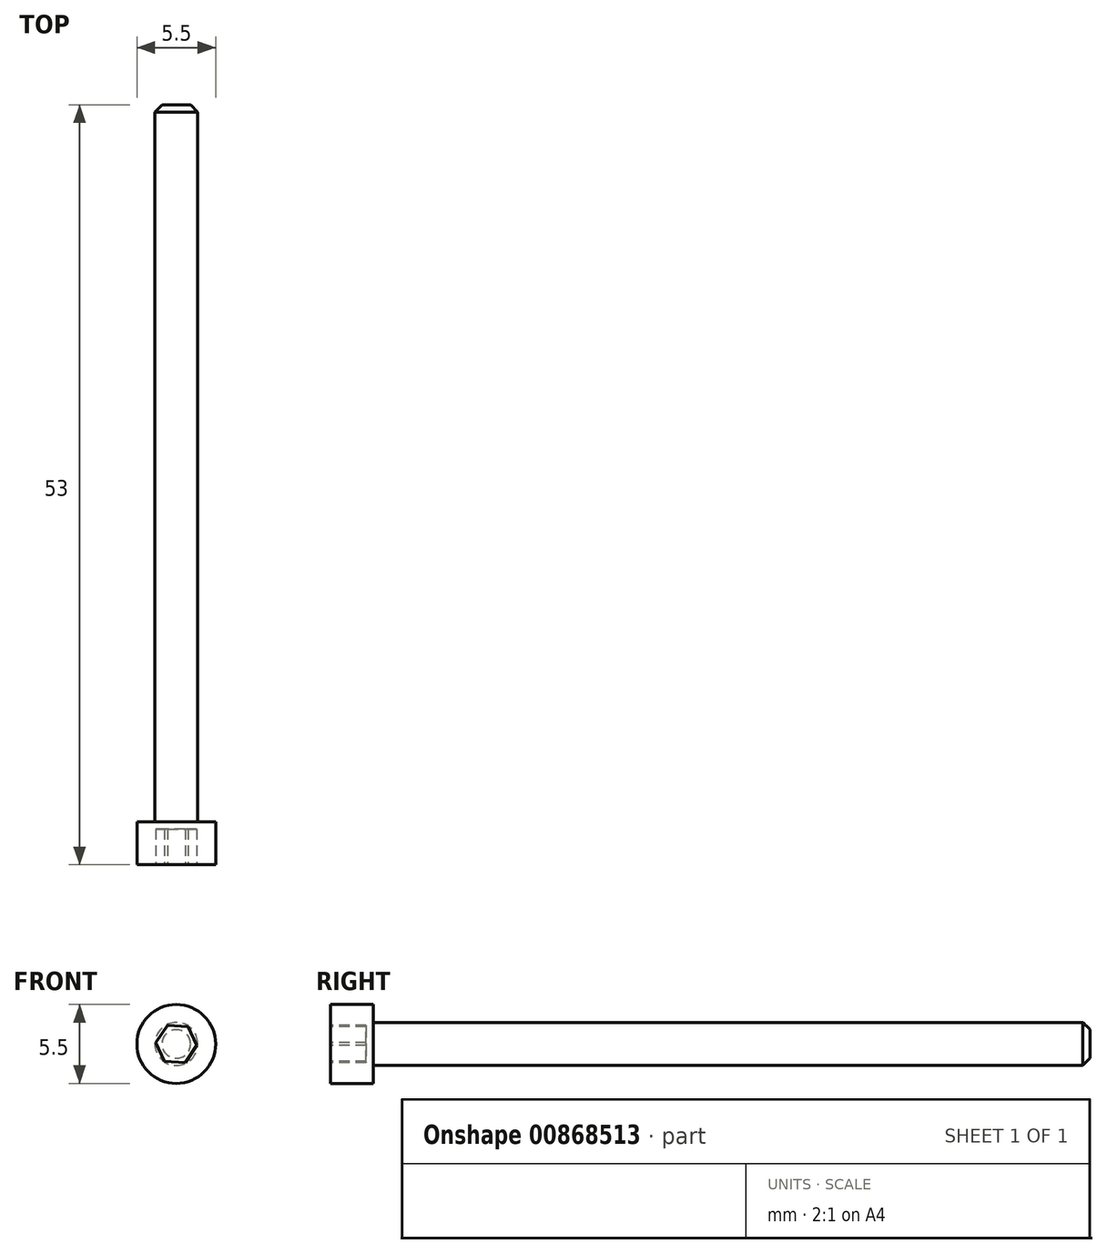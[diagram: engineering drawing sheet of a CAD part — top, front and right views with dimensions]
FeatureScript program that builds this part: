
annotation { "Feature Type Name" : "Feature", "Feature Type Description" : "" }
export const myFeature = defineFeature(function(context is Context, id is Id, definition is map)
    precondition{}
    {
        {
            assignVariable(context, id + "F0", {"name" : "Metric", "anyValue" : 3});
        }
        {
            assignVariable(context, id + "F1", {"name" : "Lenght", "anyValue" : 50});
        }
        {
            assignVariable(context, id + "F2", {"name" : "k", "anyValue" : [0, 1, 2, 3, 4, 5, 6, 0, 8][getVariable(context, 'Metric')]});
        }
        {
            var Q0;
            Q0=qCreatedBy(makeId("Front.planeOp"),FACE);
            var sketch = newSketch(context, id + "F3", { "sketchPlane" : qUnion([Q0])});
            skCircle(sketch, "E0", {"center": v(0, 0) * mm, "radius": 2.75 * mm});
            skSolve(sketch);
        }
        {
            var Q0;
            Q0 = qSketchRegion(id + "F3", true);
            extrude(context, id + "F4", {"entities" : qUnion([Q0]), "depth" : (getVariable(context, 'k')) * mm, "offsetDistance" : 25 * mm});
        }
        {
            var Q0;
            Q0=makeQuery(id+"F4.opExtrude","CAP_FACE",FACE,{"disambiguationData":[OSD([sQuery(id+"F3.wireOp",EDGE,"E0")])],"isStart":true});
            var sketch = newSketch(context, id + "F5", { "sketchPlane" : qUnion([Q0])});
            skCircle(sketch, "E1", {"center": v(0, 0) * mm, "radius": 1.5 * mm});
            skSolve(sketch);
        }
        {
            var Q0;
            Q0 = qSketchRegion(id + "F5", true);
            extrude(context, id + "F6", {"entities" : qUnion([Q0]), "operationType" : NewBodyOperationType.ADD, "depth" : (getVariable(context, 'Lenght')) * mm, "offsetDistance" : 25 * mm});
        }
        {
            var Q0;
            Q0=makeQuery(id+"F4.opExtrude","CAP_FACE",FACE,{"disambiguationData":[OSD([sQuery(id+"F3.wireOp",EDGE,"E0")])],"isStart":false});
            var sketch = newSketch(context, id + "F7", { "sketchPlane" : qUnion([Q0])});
            skCircle(sketch, "E2.cCircle", {"center": v(0, 0) * mm, "radius": 1.25 * mm, "construction": true});
            skLineSegment(sketch, "E2.0", {"start": v(-1.44, 0.11) * mm, "end": v(-0.62, 1.3) * mm});
            skLineSegment(sketch, "E2.1", {"start": v(-0.62, 1.3) * mm, "end": v(0.81, 1.2) * mm});
            skLineSegment(sketch, "E2.2", {"start": v(0.81, 1.2) * mm, "end": v(1.44, -0.11) * mm});
            skLineSegment(sketch, "E2.3", {"start": v(1.44, -0.11) * mm, "end": v(0.62, -1.3) * mm});
            skLineSegment(sketch, "E2.4", {"start": v(0.62, -1.3) * mm, "end": v(-0.81, -1.2) * mm});
            skLineSegment(sketch, "E2.5", {"start": v(-0.81, -1.2) * mm, "end": v(-1.44, 0.11) * mm});
            skPoint(sketch, "E2.0.midPoint", {"position": v(-1.03, 0.7) * mm});
            skSolve(sketch);
        }
        {
            var Q0;
            Q0 = qSketchRegion(id + "F7", true);
            extrude(context, id + "F8", {"entities" : qUnion([Q0]), "operationType" : NewBodyOperationType.REMOVE, "oppositeDirection" : true, "depth" : (getVariable(context, 'k') - 0.5) * mm, "offsetDistance" : 25 * mm});
        }
        {
            var Q0;
            Q0=makeQuery(id+"F6.opExtrude","CAP_EDGE",EDGE,{"disambiguationData":[OSD([sQuery(id+"F5.wireOp",EDGE,"E1")])],"isStart":false});
            chamfer(context, id + "F9", {"entities" : qUnion([Q0]), "width" : 0.5 * mm, "tangentPropagation" : true});
        }
    });
